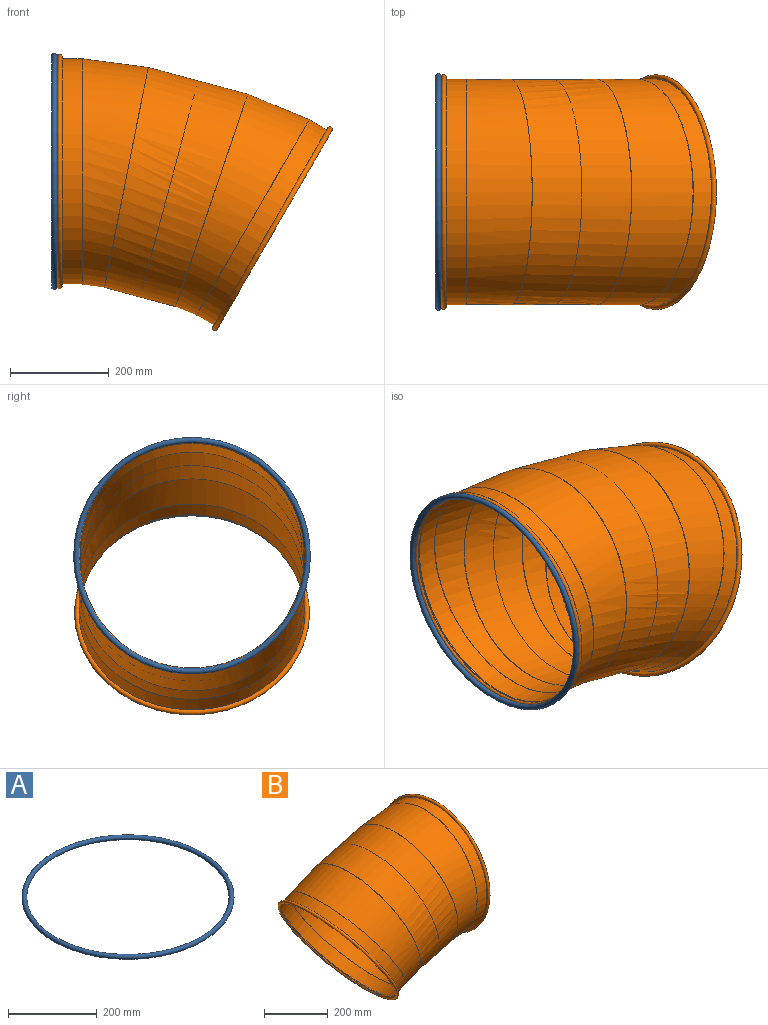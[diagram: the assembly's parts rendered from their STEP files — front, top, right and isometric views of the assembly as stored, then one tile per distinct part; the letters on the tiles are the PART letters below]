
ASSEMBLY  parts=2 mates=1
PART A: 1 faces, bbox 518.7x518.7x11 mm
  f0: torus R=234.1mm, axis (0,0,-1), area 50830.4mm2
PART B: 17 faces, bbox 577.2x914.4x596.1 mm
  f0: torus R=232.66mm, axis (-1,0,0), area 35253.2mm2, adj f1,f4
  f1: cylinder r=228.6mm len=457.2mm, axis (-1,0,0), area 65669.3mm2, adj f0,f2
  f2: bspline ~914.4x475.42mm, area 129470.7mm2, adj f1,f3
  f3: bspline ~914.4x520.93mm, area 256640.9mm2, adj f2,f11
  f4: cylinder r=228.85mm len=457.71mm, axis (-1,0,0), area 2798.1mm2, adj f0,f5
  f5: torus R=232.66mm, axis (-1,0,0), area 41400.9mm2, adj f4,f6
  f6: cylinder r=227.58mm len=455.17mm, axis (-1,0,0), area 65377.4mm2, adj f5,f7
  f7: bspline ~910.34x473.35mm, area 128894.8mm2, adj f6,f8
  f8: bspline ~910.34x518.82mm, area 127737.2mm2, adj f7,f16
  f9: torus R=232.66mm, axis (0.87,0,0.5), area 35253.2mm2, adj f10,f12
  f10: cylinder r=228.6mm len=457.2mm, axis (0.87,0,0.5), area 65669.3mm2, adj f9,f11
  f11: bspline ~914.4x449.35mm, area 129506.3mm2, adj f3,f10
  f12: cylinder r=228.85mm len=457.71mm, axis (0.87,0,0.5), area 2798.1mm2, adj f9,f13
  f13: torus R=232.66mm, axis (0.87,0,0.5), area 41400.9mm2, adj f12,f14
  f14: cylinder r=227.58mm len=455.17mm, axis (0.87,0,0.5), area 65377.4mm2, adj f13,f15
  f15: bspline ~910.34x447.51mm, area 128894.8mm2, adj f14,f16
  f16: bspline ~910.34x488.07mm, area 127737.2mm2, adj f8,f15
PLACE A rot(axis=(0,1,0),90deg) t=(-2177.35,990.63,9169.4)mm
PLACE B rot(axis=(0,0,1),180deg) t=(-2121.05,990.63,8477.68)mm
MATE fastened A.f0 <-> B.f0  axis (1,0,0) through (-2171.85,990.63,9169.4)mm
